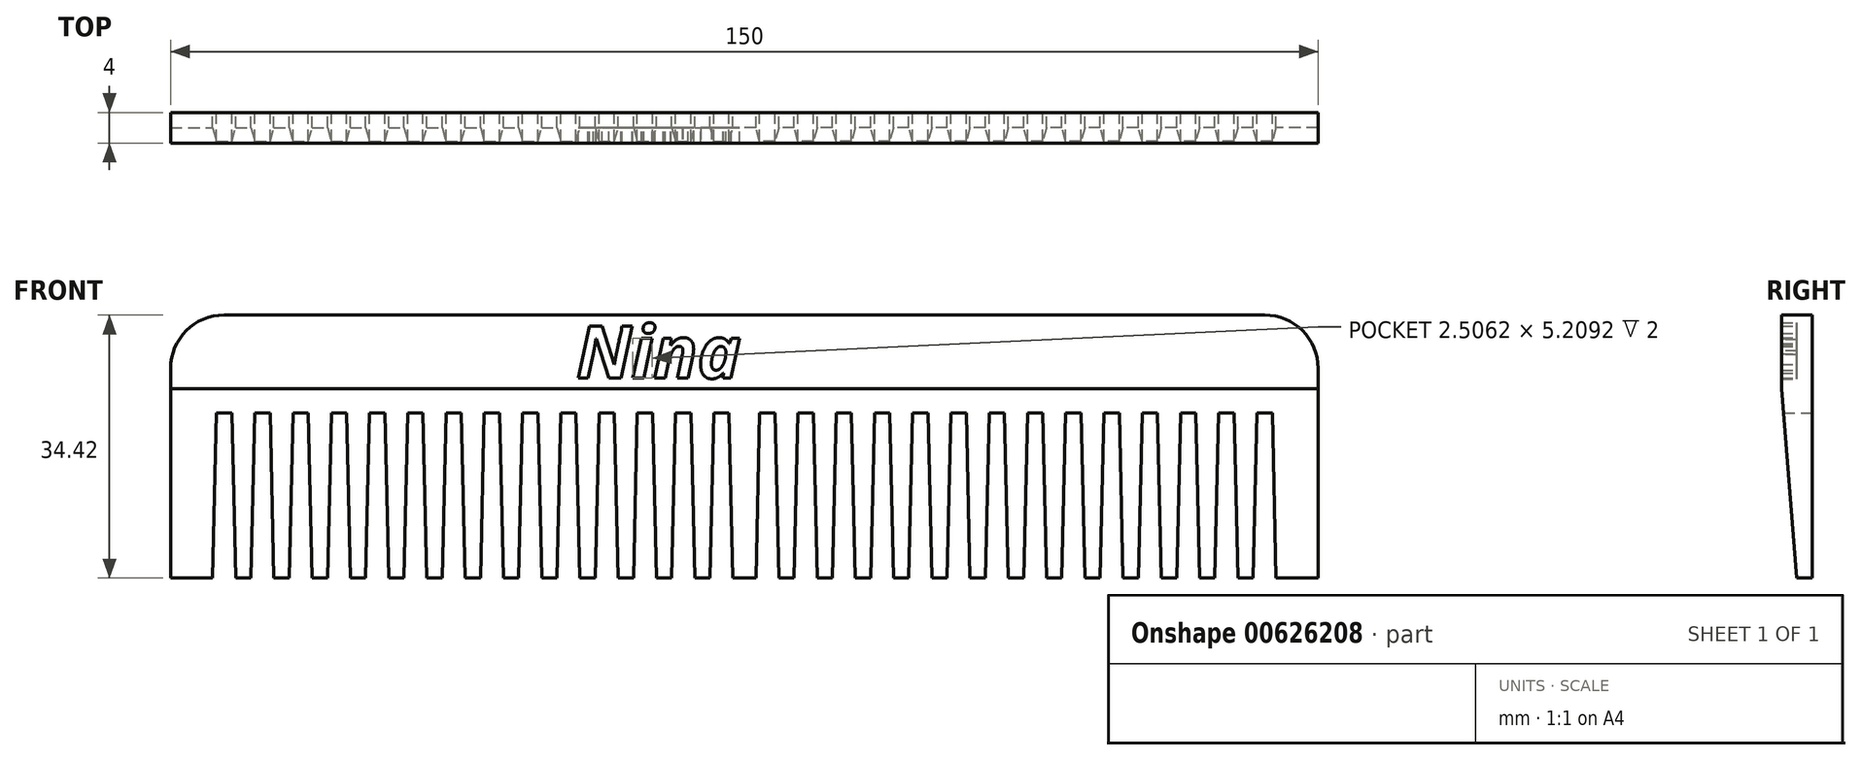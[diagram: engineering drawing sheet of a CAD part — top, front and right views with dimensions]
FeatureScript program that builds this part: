
annotation { "Feature Type Name" : "Feature", "Feature Type Description" : "" }
export const myFeature = defineFeature(function(context is Context, id is Id, definition is map)
    precondition{}
    {
        {
            var Q0;
            Q0=qCreatedBy(makeId("Front.planeOp"),FACE);
            var sketch = newSketch(context, id + "F0", { "sketchPlane" : qUnion([Q0])});
            skLineSegment(sketch, "E0.bottom", {"start": v(0, 0) * mm, "end": v(75, 0) * mm});
            skLineSegment(sketch, "E0.top", {"start": v(0, 34.42) * mm, "end": v(75, 34.42) * mm});
            skLineSegment(sketch, "E0.left", {"start": v(0, 0) * mm, "end": v(0, 34.42) * mm});
            skLineSegment(sketch, "E0.right", {"start": v(75, 0) * mm, "end": v(75, 34.42) * mm});
            skLineSegment(sketch, "E1", {"start": v(1.5, 0) * mm, "end": v(2, 21.61) * mm});
            skLineSegment(sketch, "E2", {"start": v(2, 21.61) * mm, "end": v(4, 21.61) * mm});
            skLineSegment(sketch, "E3", {"start": v(4, 21.61) * mm, "end": v(4.5, 0) * mm});
            skLineSegment(sketch, "E4", {"start": v(3, 21.61) * mm, "end": v(3, 2.01) * mm, "construction": true});
            skLineSegment(sketch, "E5.1.0.0", {"start": v(6.5, 0) * mm, "end": v(7, 21.61) * mm});
            skLineSegment(sketch, "E5.1.0.1", {"start": v(9, 21.61) * mm, "end": v(9.5, 0) * mm});
            skLineSegment(sketch, "E5.2.0.0", {"start": v(11.5, 0) * mm, "end": v(12, 21.61) * mm});
            skLineSegment(sketch, "E5.2.0.1", {"start": v(14, 21.61) * mm, "end": v(14.5, 0) * mm});
            skLineSegment(sketch, "E5.3.0.0", {"start": v(16.5, 0) * mm, "end": v(17, 21.61) * mm});
            skLineSegment(sketch, "E5.3.0.1", {"start": v(19, 21.61) * mm, "end": v(19.5, 0) * mm});
            skLineSegment(sketch, "E5.4.0.0", {"start": v(21.5, 0) * mm, "end": v(22, 21.61) * mm});
            skLineSegment(sketch, "E5.4.0.1", {"start": v(24, 21.61) * mm, "end": v(24.5, 0) * mm});
            skLineSegment(sketch, "E5.5.0.0", {"start": v(26.5, 0) * mm, "end": v(27, 21.61) * mm});
            skLineSegment(sketch, "E5.5.0.1", {"start": v(29, 21.61) * mm, "end": v(29.5, 0) * mm});
            skLineSegment(sketch, "E5.6.0.0", {"start": v(31.5, 0) * mm, "end": v(32, 21.61) * mm});
            skLineSegment(sketch, "E5.6.0.1", {"start": v(34, 21.61) * mm, "end": v(34.5, 0) * mm});
            skLineSegment(sketch, "E5.7.0.0", {"start": v(36.5, 0) * mm, "end": v(37, 21.61) * mm});
            skLineSegment(sketch, "E5.7.0.1", {"start": v(39, 21.61) * mm, "end": v(39.5, 0) * mm});
            skLineSegment(sketch, "E5.8.0.0", {"start": v(41.5, 0) * mm, "end": v(42, 21.61) * mm});
            skLineSegment(sketch, "E5.8.0.1", {"start": v(44, 21.61) * mm, "end": v(44.5, 0) * mm});
            skLineSegment(sketch, "E5.9.0.0", {"start": v(46.5, 0) * mm, "end": v(47, 21.61) * mm});
            skLineSegment(sketch, "E5.9.0.1", {"start": v(49, 21.61) * mm, "end": v(49.5, 0) * mm});
            skLineSegment(sketch, "E5.10.0.0", {"start": v(51.5, 0) * mm, "end": v(52, 21.61) * mm});
            skLineSegment(sketch, "E5.10.0.1", {"start": v(54, 21.61) * mm, "end": v(54.5, 0) * mm});
            skLineSegment(sketch, "E5.11.0.0", {"start": v(56.5, 0) * mm, "end": v(57, 21.61) * mm});
            skLineSegment(sketch, "E5.11.0.1", {"start": v(59, 21.61) * mm, "end": v(59.5, 0) * mm});
            skLineSegment(sketch, "E5.12.0.0", {"start": v(61.5, 0) * mm, "end": v(62, 21.61) * mm});
            skLineSegment(sketch, "E5.12.0.1", {"start": v(64, 21.61) * mm, "end": v(64.5, 0) * mm});
            skLineSegment(sketch, "E5.13.0.0", {"start": v(66.5, 0) * mm, "end": v(67, 21.61) * mm});
            skLineSegment(sketch, "E5.13.0.1", {"start": v(69, 21.61) * mm, "end": v(69.5, 0) * mm});
            skLineSegment(sketch, "E5.direction1", {"start": v(1.5, 0) * mm, "end": v(6.5, 0) * mm, "construction": true});
            skLineSegment(sketch, "E6", {"start": v(7, 21.61) * mm, "end": v(9, 21.61) * mm});
            skLineSegment(sketch, "E7", {"start": v(12, 21.61) * mm, "end": v(14, 21.61) * mm});
            skLineSegment(sketch, "E8", {"start": v(17, 21.61) * mm, "end": v(19, 21.61) * mm});
            skLineSegment(sketch, "E9", {"start": v(22, 21.61) * mm, "end": v(24, 21.61) * mm});
            skLineSegment(sketch, "E10", {"start": v(27, 21.61) * mm, "end": v(29, 21.61) * mm});
            skLineSegment(sketch, "E11", {"start": v(32, 21.61) * mm, "end": v(34, 21.61) * mm});
            skLineSegment(sketch, "E12", {"start": v(37, 21.61) * mm, "end": v(39, 21.61) * mm});
            skLineSegment(sketch, "E13", {"start": v(42, 21.61) * mm, "end": v(44, 21.61) * mm});
            skLineSegment(sketch, "E14", {"start": v(47, 21.61) * mm, "end": v(49, 21.61) * mm});
            skLineSegment(sketch, "E15", {"start": v(52, 21.61) * mm, "end": v(54, 21.61) * mm});
            skLineSegment(sketch, "E16", {"start": v(57, 21.61) * mm, "end": v(59, 21.61) * mm});
            skLineSegment(sketch, "E17", {"start": v(62, 21.61) * mm, "end": v(64, 21.61) * mm});
            skLineSegment(sketch, "E18", {"start": v(67, 21.61) * mm, "end": v(69, 21.61) * mm});
            skLineSegment(sketch, "E19", {"start": v(72.5, 21.61) * mm, "end": v(74.5, 21.61) * mm});
            skSolve(sketch);
        }
        {
            var Q0;
            Q0=makeQuery(id+"F0.imprint","IMPRINT",FACE,{"disambiguationData":[TD([[makeQuery(id+"F0.imprint","IMPRINT",EDGE,{"derivedFrom":sQuery(id+"F0.wireOp",EDGE,"E0.top")}),-1.0]])]});
            extrude(context, id + "F1", {"entities" : qUnion([Q0]), "endBound" : BoundingType.SYMMETRIC, "depth" : 4 * mm, "offsetDistance" : 25 * mm});
        }
        {
            var Q0;
            Q0=makeQuery(id+"F1.opExtrude","SWEPT_EDGE",EDGE,{"disambiguationData":[OSD([sQuery(id+"F0.wireOp",EDGE,"E0.top"),sQuery(id+"F0.wireOp",EDGE,"E0.right")])]});
            fillet(context, id + "F2", {"entities" : qUnion([Q0]), "radius" : 7 * mm, "tangentPropagation" : true, "allowEdgeOverflow" : false});
        }
        {
            var Q0;
            Q0=qCreatedBy(makeId("Right.planeOp"),FACE);
            var sketch = newSketch(context, id + "F3", { "sketchPlane" : qUnion([Q0])});
            skLineSegment(sketch, "E20", {"start": v(-2, 24.78) * mm, "end": v(0, 0) * mm});
            skLineSegment(sketch, "E21", {"start": v(0, 0) * mm, "end": v(-2, 0) * mm});
            skLineSegment(sketch, "E22", {"start": v(-2, 0) * mm, "end": v(-2, 24.78) * mm});
            skSolve(sketch);
        }
        {
            var Q0;
            Q0 = qSketchRegion(id + "F3", true);
            var Q1;
            Q1=sQuery(id+"F3.wireOp",EDGE,"E21");
            var Q2;
            Q2=sQuery(id+"F3.wireOp",EDGE,"E22");
            var Q3;
            Q3=sQuery(id+"F3.wireOp",EDGE,"E20");
            extrude(context, id + "F4", {"entities" : qUnion([Q0]), "operationType" : NewBodyOperationType.REMOVE, "surfaceEntities" : qUnion([Q1, Q2, Q3]), "depth" : 114.2 * mm, "offsetDistance" : 25 * mm});
        }
        {
            var Q0;
            Q0=makeQuery(id+"F1.opExtrude","SWEPT_BODY",BODY,{"disambiguationData":[OSD([sQuery(id+"F0.wireOp",EDGE,"E0.bottom"),sQuery(id+"F0.wireOp",EDGE,"E0.top"),sQuery(id+"F0.wireOp",EDGE,"E0.left"),sQuery(id+"F0.wireOp",EDGE,"E0.right"),sQuery(id+"F0.wireOp",EDGE,"E1"),sQuery(id+"F0.wireOp",EDGE,"E2"),sQuery(id+"F0.wireOp",EDGE,"E3"),sQuery(id+"F0.wireOp",EDGE,"E5.1.0.0"),sQuery(id+"F0.wireOp",EDGE,"E5.1.0.1"),sQuery(id+"F0.wireOp",EDGE,"E5.2.0.0"),sQuery(id+"F0.wireOp",EDGE,"E5.2.0.1"),sQuery(id+"F0.wireOp",EDGE,"E5.3.0.0"),sQuery(id+"F0.wireOp",EDGE,"E5.3.0.1"),sQuery(id+"F0.wireOp",EDGE,"E5.4.0.0"),sQuery(id+"F0.wireOp",EDGE,"E5.4.0.1"),sQuery(id+"F0.wireOp",EDGE,"E5.5.0.0"),sQuery(id+"F0.wireOp",EDGE,"E5.5.0.1"),sQuery(id+"F0.wireOp",EDGE,"E5.6.0.0"),sQuery(id+"F0.wireOp",EDGE,"E5.6.0.1"),sQuery(id+"F0.wireOp",EDGE,"E5.7.0.0"),sQuery(id+"F0.wireOp",EDGE,"E5.7.0.1"),sQuery(id+"F0.wireOp",EDGE,"E5.8.0.0"),sQuery(id+"F0.wireOp",EDGE,"E5.8.0.1"),sQuery(id+"F0.wireOp",EDGE,"E5.9.0.0"),sQuery(id+"F0.wireOp",EDGE,"E5.9.0.1"),sQuery(id+"F0.wireOp",EDGE,"E5.10.0.0"),sQuery(id+"F0.wireOp",EDGE,"E5.10.0.1"),sQuery(id+"F0.wireOp",EDGE,"E5.11.0.0"),sQuery(id+"F0.wireOp",EDGE,"E5.11.0.1"),sQuery(id+"F0.wireOp",EDGE,"E5.12.0.0"),sQuery(id+"F0.wireOp",EDGE,"E5.12.0.1"),sQuery(id+"F0.wireOp",EDGE,"E5.13.0.0"),sQuery(id+"F0.wireOp",EDGE,"E5.13.0.1"),sQuery(id+"F0.wireOp",EDGE,"E5.14.0.0"),sQuery(id+"F0.wireOp",EDGE,"E5.14.0.1"),sQuery(id+"F0.wireOp",EDGE,"E6"),sQuery(id+"F0.wireOp",EDGE,"E7"),sQuery(id+"F0.wireOp",EDGE,"E8"),sQuery(id+"F0.wireOp",EDGE,"E9"),sQuery(id+"F0.wireOp",EDGE,"E10"),sQuery(id+"F0.wireOp",EDGE,"E11"),sQuery(id+"F0.wireOp",EDGE,"E12"),sQuery(id+"F0.wireOp",EDGE,"E13"),sQuery(id+"F0.wireOp",EDGE,"E14"),sQuery(id+"F0.wireOp",EDGE,"E15"),sQuery(id+"F0.wireOp",EDGE,"E16"),sQuery(id+"F0.wireOp",EDGE,"E17"),sQuery(id+"F0.wireOp",EDGE,"E18"),sQuery(id+"F0.wireOp",EDGE,"E19")])]});
            var Q1;
            Q1=makeQuery(id+"F1.opExtrude","SWEPT_FACE",FACE,{"disambiguationData":[OSD([sQuery(id+"F0.wireOp",EDGE,"E0.left")])]});
            mirror(context, id + "F5", {"operationType" : NewBodyOperationType.ADD, "entities" : qUnion([Q0]), "mirrorPlane" : qUnion([Q1])});
        }
        {
            var Q0;
            Q0=qCreatedBy(makeId("Front.planeOp"),FACE);
            var sketch = newSketch(context, id + "F6", { "sketchPlane" : qUnion([Q0])});
            skText(sketch, "E23", { "text": "Nina", "fontName": "OpenSans-BoldItalic.ttf"});
            const initialGuessF6  = {"E23": [-0.02194, 0.02616, 1, 0, 0.00687]};
            skSetInitialGuess(sketch, initialGuessF6);
            skSolve(sketch);
        }
        {
            var Q0;
            Q0 = qSketchRegion(id + "F6", true);
            extrude(context, id + "F7", {"entities" : qUnion([Q0]), "operationType" : NewBodyOperationType.REMOVE, "depth" : 6.4 * mm, "offsetDistance" : 25 * mm});
        }
    });
